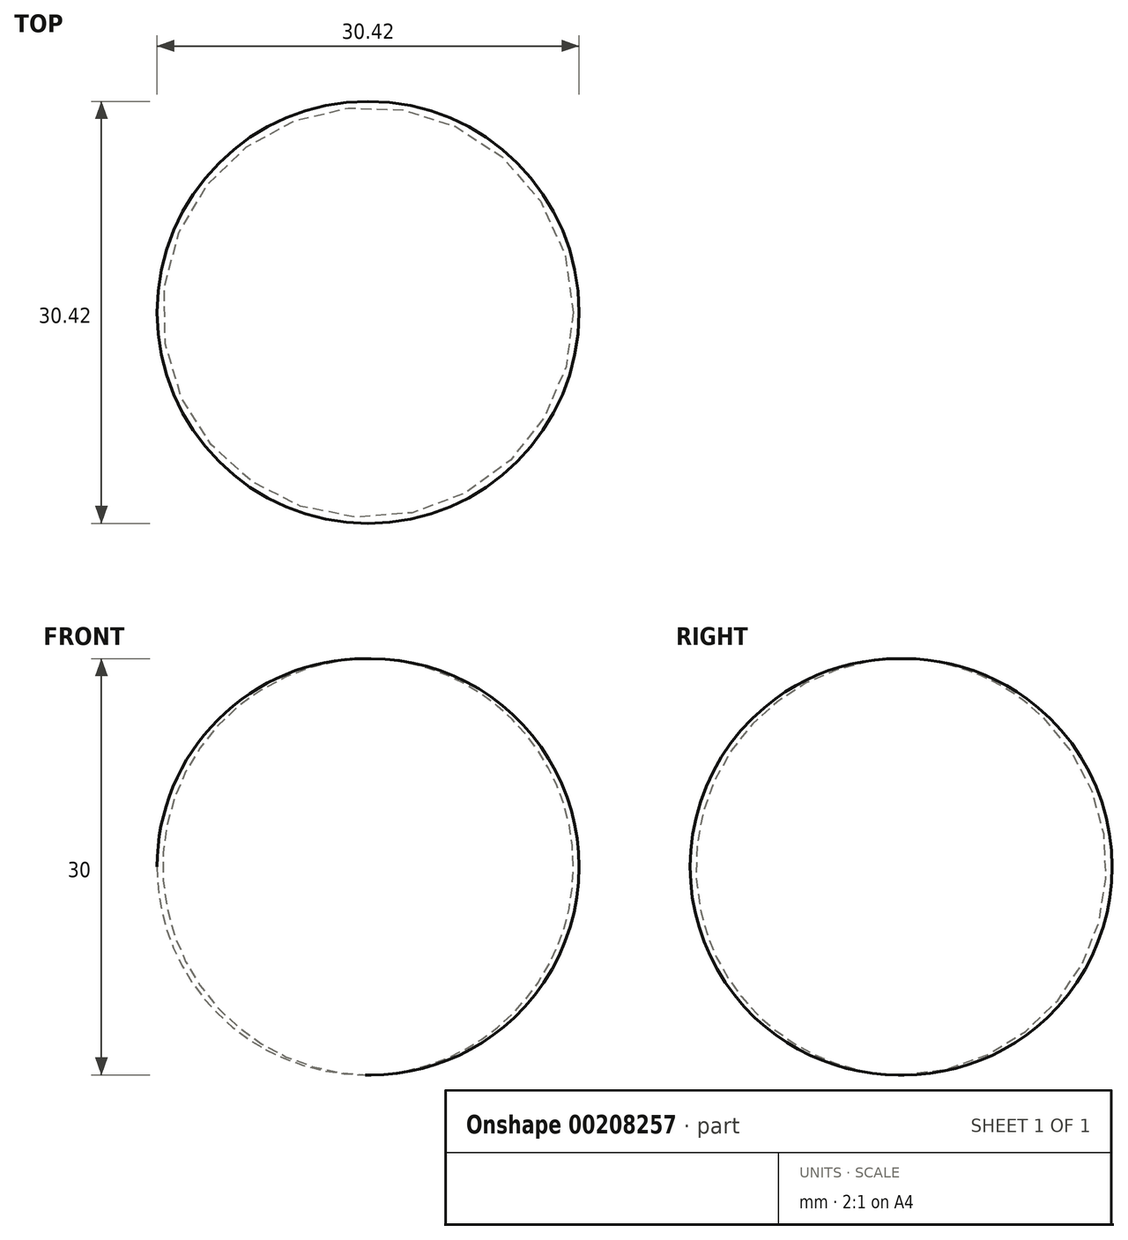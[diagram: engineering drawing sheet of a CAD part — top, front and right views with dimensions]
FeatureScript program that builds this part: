
annotation { "Feature Type Name" : "Feature", "Feature Type Description" : "" }
export const myFeature = defineFeature(function(context is Context, id is Id, definition is map)
    precondition{}
    {
        {
            var Q0;
            Q0=qCreatedBy(makeId("Front.planeOp"),FACE);
            var sketch = newSketch(context, id + "F0", { "sketchPlane" : qUnion([Q0])});
            skLineSegment(sketch, "E0", {"start": v(-24.29, 30.62) * mm, "end": v(-24.29, -19.38) * mm});
            skLineSegment(sketch, "E1", {"start": v(-24.29, 20.62) * mm, "end": v(-24.29, 30.62) * mm});
            skArc(sketch, "E2", {"start": v(-24.29, -9.38) * mm, "mid": v(-9.08, 5.62) * mm, "end": v(-24.29, 20.62) * mm});
            skSolve(sketch);
        }
        {
            var Q0;
            {var subQ0=sQuery(id+"F0.wireOp",EDGE,"E2");Q0=makeQuery(id+"F0.imprint","IMPRINT",FACE,{"disambiguationData":[TD([[makeQuery(id+"F0.imprint","IMPRINT",EDGE,{"derivedFrom":subQ0}),1.0]])]});}
            var Q1;
            Q1=sQuery(id+"F0.wireOp",EDGE,"E1");
            revolve(context, id + "F1", {"entities" : qUnion([Q0]), "axis" : qUnion([Q1]), "revolveType" : RevolveType.FULL});
        }
    });
